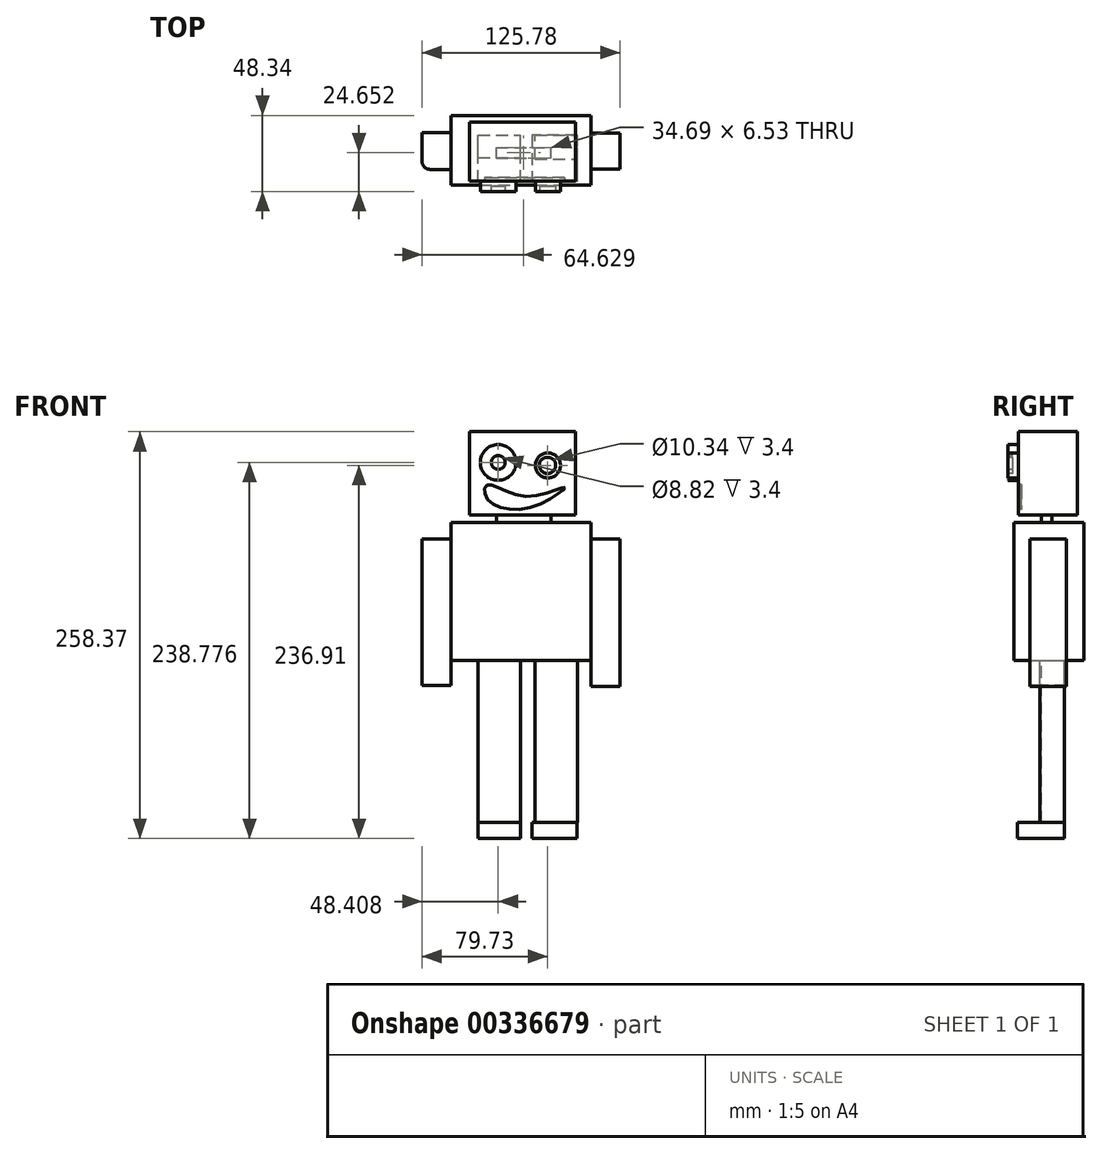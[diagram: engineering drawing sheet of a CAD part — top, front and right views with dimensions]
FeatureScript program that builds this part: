
annotation { "Feature Type Name" : "Feature", "Feature Type Description" : "" }
export const myFeature = defineFeature(function(context is Context, id is Id, definition is map)
    precondition{}
    {
        {
            var Q0;
            Q0=qCreatedBy(makeId("Front.planeOp"),FACE);
            var sketch = newSketch(context, id + "F0", { "sketchPlane" : qUnion([Q0])});
            skLineSegment(sketch, "E0.bottom", {"start": v(-32.56, 21.46) * mm, "end": v(35.05, 21.46) * mm});
            skLineSegment(sketch, "E0.top", {"start": v(-32.56, -31.61) * mm, "end": v(35.05, -31.61) * mm});
            skLineSegment(sketch, "E0.left", {"start": v(-32.56, 21.46) * mm, "end": v(-32.56, -31.61) * mm});
            skLineSegment(sketch, "E0.right", {"start": v(35.05, 21.46) * mm, "end": v(35.05, -31.61) * mm});
            skSolve(sketch);
        }
        {
            var Q0;
            Q0=makeQuery(id+"F0.imprint","IMPRINT",FACE,{"disambiguationData":[TD([[makeQuery(id+"F0.imprint","IMPRINT",EDGE,{"derivedFrom":sQuery(id+"F0.wireOp",EDGE,"E0.bottom")}),-1.0]])]});
            extrude(context, id + "F1", {"entities" : qUnion([Q0]), "depth" : 37.4 * mm});
        }
        {
            var Q0;
            Q0=makeQuery(id+"F1.opExtrude","CAP_FACE",FACE,{"disambiguationData":[OSD([sQuery(id+"F0.wireOp",EDGE,"E0.bottom"),sQuery(id+"F0.wireOp",EDGE,"E0.top"),sQuery(id+"F0.wireOp",EDGE,"E0.left"),sQuery(id+"F0.wireOp",EDGE,"E0.right")])],"isStart":false});
            var sketch = newSketch(context, id + "F2", { "sketchPlane" : qUnion([Q0])});
            skCircle(sketch, "E1", {"center": v(-14.18, 1.87) * mm, "radius": 11.35 * mm});
            skCircle(sketch, "E2", {"center": v(17.35, 0) * mm, "radius": 7.96 * mm});
            skSolve(sketch);
        }
        {
            var Q0;
            Q0 = qSketchRegion(id + "F2", true);
            extrude(context, id + "F3", {"entities" : qUnion([Q0]), "operationType" : NewBodyOperationType.ADD, "depth" : 6.7 * mm});
        }
        {
            var Q0;
            Q0=makeQuery(id+"F3.opExtrude","CAP_FACE",FACE,{"disambiguationData":[OSD([sQuery(id+"F2.wireOp",EDGE,"E1")])],"isStart":false});
            var sketch = newSketch(context, id + "F4", { "sketchPlane" : qUnion([Q0])});
            skCircle(sketch, "E3", {"center": v(-14.18, 1.87) * mm, "radius": 4.4 * mm});
            skCircle(sketch, "E4", {"center": v(17.14, 0) * mm, "radius": 5.17 * mm});
            skSolve(sketch);
        }
        {
            var Q0;
            Q0 = qSketchRegion(id + "F4", true);
            extrude(context, id + "F5", {"entities" : qUnion([Q0]), "operationType" : NewBodyOperationType.REMOVE, "oppositeDirection" : true, "depth" : 3.4 * mm});
        }
        {
            var Q0;
            Q0=makeQuery(id+"F1.opExtrude","CAP_FACE",FACE,{"disambiguationData":[OSD([sQuery(id+"F0.wireOp",EDGE,"E0.bottom"),sQuery(id+"F0.wireOp",EDGE,"E0.top"),sQuery(id+"F0.wireOp",EDGE,"E0.left"),sQuery(id+"F0.wireOp",EDGE,"E0.right")])],"isStart":false});
            var sketch = newSketch(context, id + "F6", { "sketchPlane" : qUnion([Q0])});
            skFitSpline(sketch, "E5", {"points": [v(-21.27, -12.5) * mm, v(3.36, -19.6) * mm, v(27.8, -14) * mm, v(7.84, -26.31) * mm, v(-21.09, -21.27) * mm, v(-21.27, -12.5) * mm]});
            skSolve(sketch);
        }
        {
            var Q0;
            Q0 = qSketchRegion(id + "F6", true);
            extrude(context, id + "F7", {"entities" : qUnion([Q0]), "operationType" : NewBodyOperationType.REMOVE, "oppositeDirection" : true, "depth" : 2.1 * mm});
        }
        {
            var Q0;
            Q0=makeQuery(id+"F1.opExtrude","SWEPT_FACE",FACE,{"disambiguationData":[OSD([sQuery(id+"F0.wireOp",EDGE,"E0.top")])]});
            var sketch = newSketch(context, id + "F8", { "sketchPlane" : qUnion([Q0])});
            skLineSegment(sketch, "E6.bottom", {"start": v(-15.3, 22.71) * mm, "end": v(19.38, 22.71) * mm});
            skLineSegment(sketch, "E6.top", {"start": v(-15.3, 16.18) * mm, "end": v(19.38, 16.18) * mm});
            skLineSegment(sketch, "E6.left", {"start": v(-15.3, 22.71) * mm, "end": v(-15.3, 16.18) * mm});
            skLineSegment(sketch, "E6.right", {"start": v(19.38, 22.71) * mm, "end": v(19.38, 16.18) * mm});
            skSolve(sketch);
        }
        {
            var Q0;
            Q0 = qSketchRegion(id + "F8", true);
            extrude(context, id + "F9", {"entities" : qUnion([Q0]), "operationType" : NewBodyOperationType.ADD, "depth" : 4.6 * mm});
        }
        {
            var Q0;
            Q0=makeQuery(id+"F9.opExtrude","CAP_FACE",FACE,{"disambiguationData":[OSD([sQuery(id+"F8.wireOp",EDGE,"E6.bottom"),sQuery(id+"F8.wireOp",EDGE,"E6.top"),sQuery(id+"F8.wireOp",EDGE,"E6.left"),sQuery(id+"F8.wireOp",EDGE,"E6.right")])],"isStart":false});
            var sketch = newSketch(context, id + "F10", { "sketchPlane" : qUnion([Q0])});
            skLineSegment(sketch, "E7.bottom", {"start": v(-44, 40.06) * mm, "end": v(44.8, 40.06) * mm});
            skLineSegment(sketch, "E7.top", {"start": v(-44, -4.24) * mm, "end": v(44.8, -4.24) * mm});
            skLineSegment(sketch, "E7.left", {"start": v(-44, 40.06) * mm, "end": v(-44, -4.24) * mm});
            skLineSegment(sketch, "E7.right", {"start": v(44.8, 40.06) * mm, "end": v(44.8, -4.24) * mm});
            skSolve(sketch);
        }
        {
            var Q0;
            Q0 = qSketchRegion(id + "F10", true);
            extrude(context, id + "F11", {"entities" : qUnion([Q0]), "operationType" : NewBodyOperationType.ADD, "depth" : 87.7 * mm});
        }
        {
            var Q0;
            Q0=makeQuery(id+"F11.opExtrude","SWEPT_FACE",FACE,{"disambiguationData":[OSD([sQuery(id+"F10.wireOp",EDGE,"E7.right")])]});
            var sketch = newSketch(context, id + "F12", { "sketchPlane" : qUnion([Q0])});
            skLineSegment(sketch, "E8.bottom", {"start": v(-29.86, -46.83) * mm, "end": v(-6.87, -46.83) * mm});
            skLineSegment(sketch, "E8.top", {"start": v(-29.86, -140.43) * mm, "end": v(-6.87, -140.43) * mm});
            skLineSegment(sketch, "E8.left", {"start": v(-29.86, -46.83) * mm, "end": v(-29.86, -140.43) * mm});
            skLineSegment(sketch, "E8.right", {"start": v(-6.87, -46.83) * mm, "end": v(-6.87, -140.43) * mm});
            skSolve(sketch);
        }
        {
            var Q0;
            Q0 = qSketchRegion(id + "F12", true);
            extrude(context, id + "F13", {"entities" : qUnion([Q0]), "operationType" : NewBodyOperationType.ADD, "depth" : 18.4 * mm});
        }
        {
            var Q0;
            Q0=makeQuery(id+"F11.opExtrude","SWEPT_FACE",FACE,{"disambiguationData":[OSD([sQuery(id+"F10.wireOp",EDGE,"E7.left")])]});
            var sketch = newSketch(context, id + "F14", { "sketchPlane" : qUnion([Q0])});
            skLineSegment(sketch, "E9.bottom", {"start": v(6.7, -46.65) * mm, "end": v(30.02, -46.65) * mm});
            skLineSegment(sketch, "E9.top", {"start": v(6.7, -139.92) * mm, "end": v(30.02, -139.92) * mm});
            skLineSegment(sketch, "E9.left", {"start": v(6.7, -46.65) * mm, "end": v(6.7, -139.92) * mm});
            skLineSegment(sketch, "E9.right", {"start": v(30.02, -46.65) * mm, "end": v(30.02, -139.92) * mm});
            skSolve(sketch);
        }
        {
            var Q0;
            {var subQ0=sQuery(id+"F14.wireOp",EDGE,"E9.bottom");Q0=makeQuery(id+"F14.imprint","IMPRINT",FACE,{"disambiguationData":[TD([[makeQuery(id+"F14.imprint","IMPRINT",EDGE,{"derivedFrom":subQ0}),-1.0]])]});}
            var Q1;
            {var subQ0=sQuery(id+"F14.wireOp",EDGE,"E9.top");Q1=makeQuery(id+"F14.imprint","IMPRINT",FACE,{"disambiguationData":[TD([[makeQuery(id+"F14.imprint","IMPRINT",EDGE,{"derivedFrom":subQ0}),1.0]])]});}
            extrude(context, id + "F15", {"entities" : qUnion([Q0, Q1]), "operationType" : NewBodyOperationType.ADD, "depth" : 18.6 * mm});
        }
        {
            var Q0;
            Q0=makeQuery(id+"F11.opExtrude","CAP_FACE",FACE,{"disambiguationData":[OSD([sQuery(id+"F10.wireOp",EDGE,"E7.bottom"),sQuery(id+"F10.wireOp",EDGE,"E7.top"),sQuery(id+"F10.wireOp",EDGE,"E7.left"),sQuery(id+"F10.wireOp",EDGE,"E7.right")])],"isStart":false});
            var sketch = newSketch(context, id + "F16", { "sketchPlane" : qUnion([Q0])});
            skLineSegment(sketch, "E10.bottom", {"start": v(-27.03, 22.65) * mm, "end": v(0, 22.65) * mm});
            skLineSegment(sketch, "E10.top", {"start": v(-27.03, 8.2) * mm, "end": v(0, 8.2) * mm});
            skLineSegment(sketch, "E10.left", {"start": v(-27.03, 22.65) * mm, "end": v(-27.03, 8.2) * mm});
            skLineSegment(sketch, "E10.right", {"start": v(0, 22.65) * mm, "end": v(0, 8.2) * mm});
            skLineSegment(sketch, "E11.bottom", {"start": v(9.26, 23.66) * mm, "end": v(36.03, 23.66) * mm});
            skLineSegment(sketch, "E11.top", {"start": v(9.26, 8.2) * mm, "end": v(36.03, 8.2) * mm});
            skLineSegment(sketch, "E11.left", {"start": v(9.26, 23.66) * mm, "end": v(9.26, 8.2) * mm});
            skLineSegment(sketch, "E11.right", {"start": v(36.03, 23.66) * mm, "end": v(36.03, 8.2) * mm});
            skSolve(sketch);
        }
        {
            var Q0;
            Q0 = qSketchRegion(id + "F16", true);
            extrude(context, id + "F17", {"entities" : qUnion([Q0]), "operationType" : NewBodyOperationType.ADD, "depth" : 103 * mm});
        }
        {
            var Q0;
            Q0=makeQuery(id+"F17.opExtrude","CAP_FACE",FACE,{"disambiguationData":[OSD([sQuery(id+"F16.wireOp",EDGE,"E10.bottom"),sQuery(id+"F16.wireOp",EDGE,"E10.top"),sQuery(id+"F16.wireOp",EDGE,"E10.left"),sQuery(id+"F16.wireOp",EDGE,"E10.right")])],"isStart":false});
            var sketch = newSketch(context, id + "F18", { "sketchPlane" : qUnion([Q0])});
            skLineSegment(sketch, "E12.bottom", {"start": v(-27.03, 8.2) * mm, "end": v(0, 8.2) * mm});
            skLineSegment(sketch, "E12.top", {"start": v(-27.03, 37.89) * mm, "end": v(0, 37.89) * mm});
            skLineSegment(sketch, "E12.left", {"start": v(-27.03, 8.2) * mm, "end": v(-27.03, 37.89) * mm});
            skLineSegment(sketch, "E12.right", {"start": v(0, 8.2) * mm, "end": v(0, 37.89) * mm});
            skLineSegment(sketch, "E13.bottom", {"start": v(36.02, 8.2) * mm, "end": v(7.2, 8.2) * mm});
            skLineSegment(sketch, "E13.top", {"start": v(36.02, 37.89) * mm, "end": v(7.2, 37.89) * mm});
            skLineSegment(sketch, "E13.left", {"start": v(36.02, 8.2) * mm, "end": v(36.02, 37.89) * mm});
            skLineSegment(sketch, "E13.right", {"start": v(7.2, 8.2) * mm, "end": v(7.2, 37.89) * mm});
            skSolve(sketch);
        }
        {
            var Q0;
            Q0 = qSketchRegion(id + "F18", true);
            extrude(context, id + "F19", {"entities" : qUnion([Q0]), "operationType" : NewBodyOperationType.ADD, "depth" : 10 * mm});
        }
        {
            var Q0;
            Q0=makeQuery(id+"F15.opExtrude","CAP_EDGE",EDGE,{"disambiguationData":[OSD([sQuery(id+"F14.wireOp",EDGE,"E9.right")])],"isStart":false});
            fillet(context, id + "F20", {"entities" : qUnion([Q0]), "radius" : 5 * mm, "tangentPropagation" : true, "allowEdgeOverflow" : false});
        }
    });
